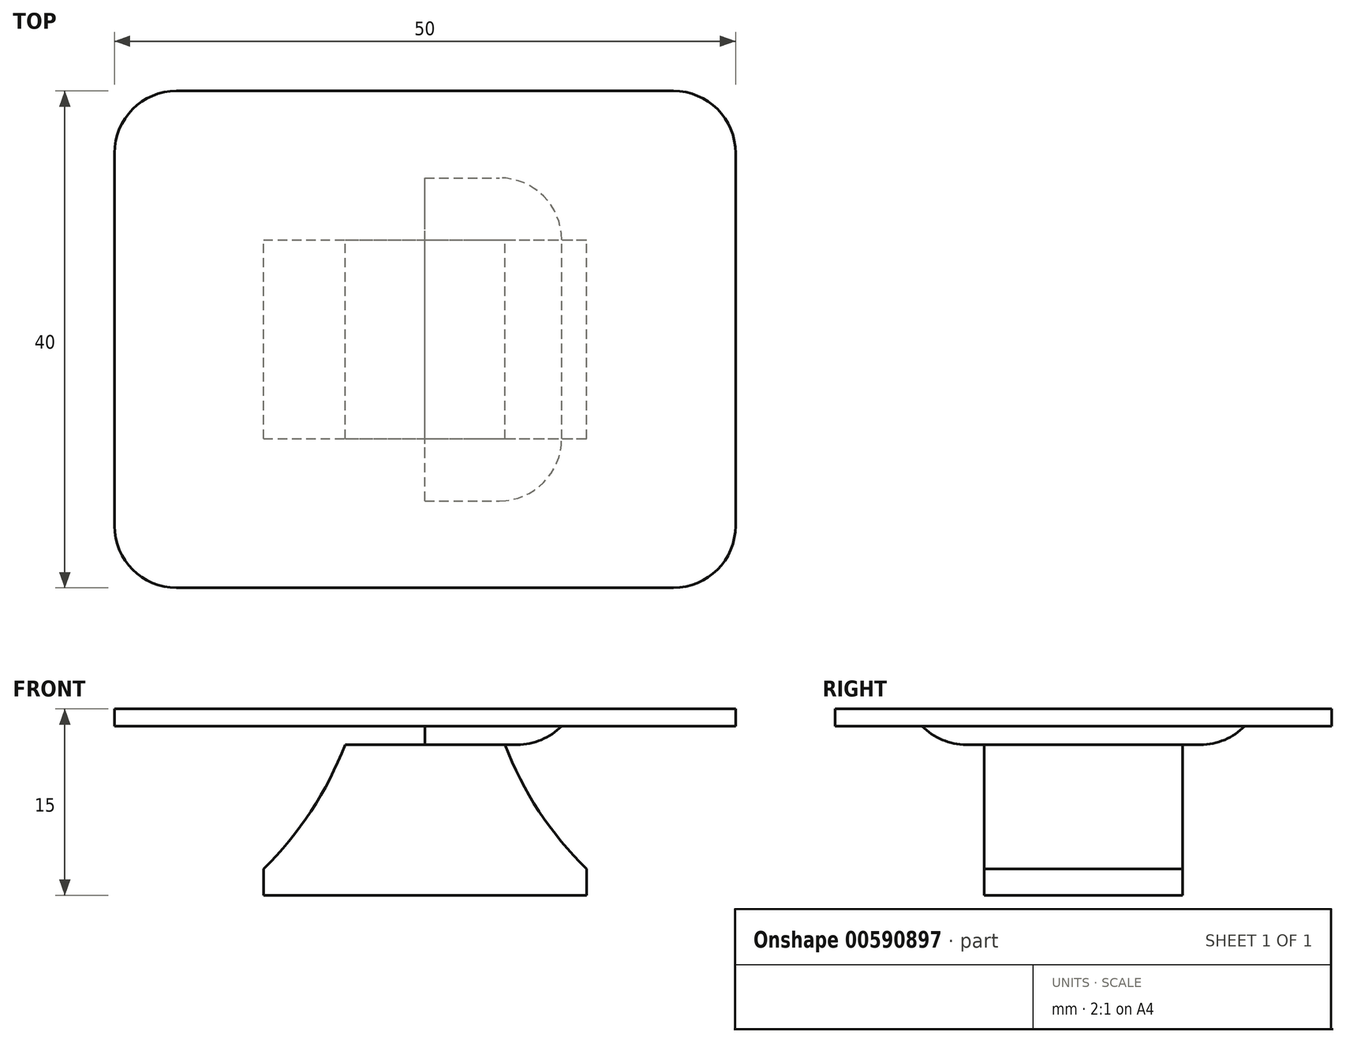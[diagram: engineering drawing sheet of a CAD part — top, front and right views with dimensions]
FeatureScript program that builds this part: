
annotation { "Feature Type Name" : "Feature", "Feature Type Description" : "" }
export const myFeature = defineFeature(function(context is Context, id is Id, definition is map)
    precondition{}
    {
        {
            var Q0;
            Q0=qCreatedBy(makeId("Front.planeOp"),FACE);
            var sketch = newSketch(context, id + "F0", { "sketchPlane" : qUnion([Q0])});
            skLineSegment(sketch, "E0.bottom", {"start": v(0, 15) * mm, "end": v(-25, 15) * mm});
            skLineSegment(sketch, "E0.top", {"start": v(0, 13.62) * mm, "end": v(-25, 13.62) * mm});
            skLineSegment(sketch, "E0.left", {"start": v(0, 15) * mm, "end": v(0, 13.62) * mm});
            skLineSegment(sketch, "E0.right", {"start": v(-25, 15) * mm, "end": v(-25, 13.62) * mm});
            skLineSegment(sketch, "E1.bottom", {"start": v(-11, 13.62) * mm, "end": v(0, 13.62) * mm});
            skLineSegment(sketch, "E1.top", {"start": v(-11, 12.12) * mm, "end": v(0, 12.12) * mm});
            skLineSegment(sketch, "E1.left", {"start": v(-11, 13.62) * mm, "end": v(-11, 12.12) * mm});
            skLineSegment(sketch, "E1.right", {"start": v(0, 13.62) * mm, "end": v(0, 12.12) * mm});
            skLineSegment(sketch, "E2.bottom", {"start": v(-13, 2.12) * mm, "end": v(0, 2.12) * mm});
            skLineSegment(sketch, "E2.top", {"start": v(-13, 0) * mm, "end": v(0, 0) * mm});
            skLineSegment(sketch, "E2.left", {"start": v(-13, 2.12) * mm, "end": v(-13, 0) * mm});
            skLineSegment(sketch, "E2.right", {"start": v(0, 2.12) * mm, "end": v(0, 0) * mm});
            skLineSegment(sketch, "E3", {"start": v(0, 15) * mm, "end": v(0, 0) * mm});
            skLineSegment(sketch, "E4.MirrorCS", {"start": v(13, 2.12) * mm, "end": v(13, 0) * mm});
            skLineSegment(sketch, "E5.MirrorCS", {"start": v(25, 15) * mm, "end": v(25, 13.62) * mm});
            skLineSegment(sketch, "E6.MirrorCS", {"start": v(11, 13.62) * mm, "end": v(11, 12.12) * mm});
            skLineSegment(sketch, "E7.MirrorCS", {"start": v(13, 2.12) * mm, "end": v(0, 2.12) * mm});
            skLineSegment(sketch, "E8.MirrorCS", {"start": v(13, 0) * mm, "end": v(0, 0) * mm});
            skLineSegment(sketch, "E9.MirrorCS", {"start": v(0, 15) * mm, "end": v(25, 15) * mm});
            skLineSegment(sketch, "E10.MirrorCS", {"start": v(0, 13.62) * mm, "end": v(25, 13.62) * mm});
            skLineSegment(sketch, "E11.MirrorCS", {"start": v(11, 12.12) * mm, "end": v(0, 12.12) * mm});
            skLineSegment(sketch, "E12.MirrorCS", {"start": v(11, 13.62) * mm, "end": v(0, 13.62) * mm});
            skArc(sketch, "E13", {"start": v(-13, 2.12) * mm, "mid": v(-9.17, 6.76) * mm, "end": v(-6.44, 12.12) * mm});
            skArc(sketch, "E14.MirrorCS", {"start": v(13, 2.12) * mm, "mid": v(9.17, 6.76) * mm, "end": v(6.44, 12.12) * mm});
            skSolve(sketch);
        }
        {
            var Q0;
            Q0=makeQuery(id+"F0.imprint","IMPRINT",FACE,{"disambiguationData":[TD([[makeQuery(id+"F0.imprint","IMPRINT",EDGE,{"derivedFrom":sQuery(id+"F0.wireOp",EDGE,"E0.bottom")}),1.0]])]});
            var Q1;
            Q1=makeQuery(id+"F0.imprint","IMPRINT",FACE,{"disambiguationData":[TD([[makeQuery(id+"F0.imprint","IMPRINT",EDGE,{"derivedFrom":sQuery(id+"F0.wireOp",EDGE,"E0.left")}),1.0]])]});
            extrude(context, id + "F1", {"entities" : qUnion([Q0, Q1]), "endBound" : BoundingType.SYMMETRIC, "depth" : 40 * mm, "offsetDistance" : 25 * mm});
        }
        {
            var Q0;
            Q0=makeQuery(id+"F0.imprint","IMPRINT",FACE,{"disambiguationData":[TD([[makeQuery(id+"F0.imprint","IMPRINT",EDGE,{"derivedFrom":sQuery(id+"F0.wireOp",EDGE,"E1.bottom")}),-1.0]])]});
            var Q1;
            {var subQ3=sQuery(id+"F0.wireOp",EDGE,"E6.MirrorCS");Q1=makeQuery(id+"F0.imprint","IMPRINT",FACE,{"disambiguationData":[TD([[makeQuery(id+"F0.imprint","IMPRINT",EDGE,{"derivedFrom":subQ3}),-1.0]])]});}
            var Q2;
            Q2=makeQuery(id+"F0.imprint","IMPRINT",FACE,{"disambiguationData":[TD([[makeQuery(id+"F0.imprint","IMPRINT",EDGE,{"derivedFrom":sQuery(id+"F0.wireOp",EDGE,"E2.bottom")}),-1.0]])]});
            var Q3;
            Q3=makeQuery(id+"F0.imprint","IMPRINT",FACE,{"disambiguationData":[TD([[makeQuery(id+"F0.imprint","IMPRINT",EDGE,{"derivedFrom":sQuery(id+"F0.wireOp",EDGE,"E4.MirrorCS")}),-1.0]])]});
            extrude(context, id + "F2", {"entities" : qUnion([Q0, Q1, Q2, Q3]), "operationType" : NewBodyOperationType.ADD, "endBound" : BoundingType.SYMMETRIC, "depth" : 26 * mm, "offsetDistance" : 25 * mm});
        }
        {
            var Q0;
            Q0=makeQuery(id+"F2.opExtrude","CAP_EDGE",EDGE,{"disambiguationData":[OSD([sQuery(id+"F0.wireOp",EDGE,"E2.left")])],"isStart":true});
            var Q1;
            Q1=makeQuery(id+"F2.opExtrude","CAP_EDGE",EDGE,{"disambiguationData":[OSD([sQuery(id+"F0.wireOp",EDGE,"E2.left")])],"isStart":false});
            var Q2;
            Q2=makeQuery(id+"F2.opExtrude","CAP_EDGE",EDGE,{"disambiguationData":[OSD([sQuery(id+"F0.wireOp",EDGE,"E4.MirrorCS")])],"isStart":false});
            var Q3;
            Q3=makeQuery(id+"F2.opExtrude","CAP_EDGE",EDGE,{"disambiguationData":[OSD([sQuery(id+"F0.wireOp",EDGE,"E4.MirrorCS")])],"isStart":true});
            fillet(context, id + "F3", {"entities" : qUnion([Q0, Q1, Q2, Q3]), "radius" : 5 * mm, "tangentPropagation" : true, "allowEdgeOverflow" : false});
        }
        {
            var Q0;
            Q0=makeQuery(id+"F1.opExtrude","CAP_EDGE",EDGE,{"disambiguationData":[OSD([sQuery(id+"F0.wireOp",EDGE,"E0.right")])],"isStart":false});
            var Q1;
            Q1=makeQuery(id+"F1.opExtrude","CAP_EDGE",EDGE,{"disambiguationData":[OSD([sQuery(id+"F0.wireOp",EDGE,"E0.right")])],"isStart":true});
            var Q2;
            Q2=makeQuery(id+"F1.opExtrude","CAP_EDGE",EDGE,{"disambiguationData":[OSD([sQuery(id+"F0.wireOp",EDGE,"E5.MirrorCS")])],"isStart":false});
            var Q3;
            Q3=makeQuery(id+"F1.opExtrude","CAP_EDGE",EDGE,{"disambiguationData":[OSD([sQuery(id+"F0.wireOp",EDGE,"E5.MirrorCS")])],"isStart":true});
            fillet(context, id + "F4", {"entities" : qUnion([Q0, Q1, Q2, Q3]), "radius" : 5 * mm, "tangentPropagation" : true, "allowEdgeOverflow" : false});
        }
        {
            var Q0;
            Q0=makeQuery(id+"F2.opExtrude","SWEPT_BODY",BODY,{"disambiguationData":[OSD([sQuery(id+"F0.wireOp",EDGE,"E2.bottom"),sQuery(id+"F0.wireOp",EDGE,"E2.top"),sQuery(id+"F0.wireOp",EDGE,"E2.left"),sQuery(id+"F0.wireOp",EDGE,"E4.MirrorCS"),sQuery(id+"F0.wireOp",EDGE,"E7.MirrorCS"),sQuery(id+"F0.wireOp",EDGE,"E8.MirrorCS")])]});
            deleteBodies(context, id + "F5", {"entities" : qUnion([Q0])});
        }
        {
            var Q0;
            Q0=makeQuery(id+"F0.imprint","IMPRINT",FACE,{"disambiguationData":[TD([[makeQuery(id+"F0.imprint","IMPRINT",EDGE,{"derivedFrom":sQuery(id+"F0.wireOp",EDGE,"E2.bottom")}),1.0]])]});
            var Q1;
            Q1=makeQuery(id+"F0.imprint","IMPRINT",FACE,{"disambiguationData":[TD([[makeQuery(id+"F0.imprint","IMPRINT",EDGE,{"derivedFrom":sQuery(id+"F0.wireOp",EDGE,"E2.bottom")}),-1.0]])]});
            var Q2;
            {var subQ0=sQuery(id+"F0.wireOp",EDGE,"E3");Q2=makeQuery(id+"F0.imprint","IMPRINT",FACE,{"disambiguationData":[TD([[makeQuery(id+"F0.imprint","IMPRINT",EDGE,{"derivedFrom":subQ0}),1.0]])]});}
            var Q3;
            Q3=makeQuery(id+"F0.imprint","IMPRINT",FACE,{"disambiguationData":[TD([[makeQuery(id+"F0.imprint","IMPRINT",EDGE,{"derivedFrom":sQuery(id+"F0.wireOp",EDGE,"E4.MirrorCS")}),-1.0]])]});
            extrude(context, id + "F6", {"entities" : qUnion([Q0, Q1, Q2, Q3]), "operationType" : NewBodyOperationType.ADD, "endBound" : BoundingType.SYMMETRIC, "depth" : 16 * mm, "offsetDistance" : 25 * mm});
        }
        {
            var Q0;
            Q0=makeQuery(id+"F2.opExtrude","CAP_EDGE",EDGE,{"disambiguationData":[OSD([sQuery(id+"F0.wireOp",EDGE,"E1.left")])],"isStart":false});
            var Q1;
            Q1=makeQuery(id+"F2.opExtrude","CAP_EDGE",EDGE,{"disambiguationData":[OSD([sQuery(id+"F0.wireOp",EDGE,"E1.left")])],"isStart":true});
            var Q2;
            Q2=makeQuery(id+"F2.opExtrude","CAP_EDGE",EDGE,{"disambiguationData":[OSD([sQuery(id+"F0.wireOp",EDGE,"E6.MirrorCS")])],"isStart":false});
            var Q3;
            Q3=makeQuery(id+"F2.opExtrude","CAP_EDGE",EDGE,{"disambiguationData":[OSD([sQuery(id+"F0.wireOp",EDGE,"E6.MirrorCS")])],"isStart":true});
            fillet(context, id + "F7", {"entities" : qUnion([Q0, Q1, Q2, Q3]), "radius" : 5 * mm, "tangentPropagation" : true, "allowEdgeOverflow" : false});
        }
        {
            var Q0;
            Q0=makeQuery(id+"F2.opExtrude","CAP_EDGE",EDGE,{"disambiguationData":[OSD([sQuery(id+"F0.wireOp",EDGE,"E1.top"),sQuery(id+"F0.wireOp",EDGE,"E11.MirrorCS")])],"isStart":false});
            fillet(context, id + "F8", {"entities" : qUnion([Q0]), "radius" : 5 * mm, "tangentPropagation" : true, "allowEdgeOverflow" : false});
        }
    });
